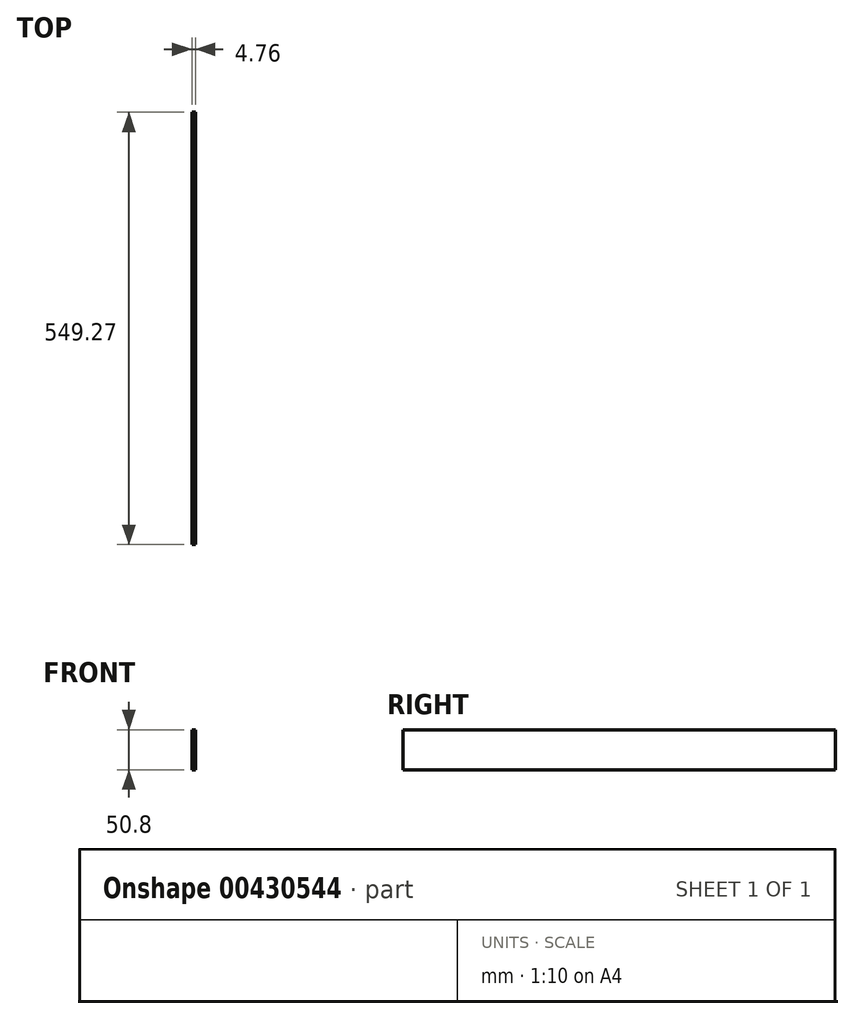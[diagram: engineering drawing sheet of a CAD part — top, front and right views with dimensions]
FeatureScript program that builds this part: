
annotation { "Feature Type Name" : "Feature", "Feature Type Description" : "" }
export const myFeature = defineFeature(function(context is Context, id is Id, definition is map)
    precondition{}
    {
        {
            var Q0;
            Q0=qCreatedBy(makeId("Right.planeOp"),FACE);
            var sketch = newSketch(context, id + "F0", { "sketchPlane" : qUnion([Q0])});
            skLineSegment(sketch, "E0.bottom", {"start": v(-227.5, -86.48) * mm, "end": v(321.77, -86.48) * mm});
            skLineSegment(sketch, "E0.top", {"start": v(-227.5, -137.28) * mm, "end": v(321.77, -137.28) * mm});
            skLineSegment(sketch, "E0.left", {"start": v(-227.5, -86.48) * mm, "end": v(-227.5, -137.28) * mm});
            skLineSegment(sketch, "E0.right", {"start": v(321.77, -86.48) * mm, "end": v(321.77, -137.28) * mm});
            skSolve(sketch);
        }
        {
            var Q0;
            Q0=makeQuery(id+"F0.imprint","IMPRINT",FACE,{"disambiguationData":[TD([[makeQuery(id+"F0.imprint","IMPRINT",EDGE,{"derivedFrom":sQuery(id+"F0.wireOp",EDGE,"E0.bottom")}),-1.0]])]});
            extrude(context, id + "F1", {"entities" : qUnion([Q0]), "depth" : 4.76 * mm});
        }
    });
